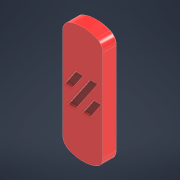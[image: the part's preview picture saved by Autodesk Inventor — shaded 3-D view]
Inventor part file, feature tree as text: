
AUTODESK INVENTOR PART (.ipt)
format: ipt  version: 2022.1 (Build 261234000, 234)  size: 317,440 bytes
history: native  units: mm
features: sketch x8, extrude x7, projected_geometry x6, direct_edit x5, move_body x5, reference x4, other x3, hole x2, chamfer x2, fillet x1, plane x1, delete_face x1
ambient origin geometry x8: Origin, YZ Plane, XZ Plane, XY Plane, X Axis, Y Axis, Z Axis, Center Point
bodies: Volumenkörper1 (feature_tree)
feature tree (45):
  extrude  "Extrusion1"  Depth=4.0mm TaperAngle=0.0deg
  extrude  "Extrusion2"  Depth=3.2mm
  hole  "Bohrung1"  [1 undecoded]
  sketch  "Skizze4"  dims[d109=2.156321mm d110=2.156321mm]
  direct_edit  "Direktbearbeitung1"
  fillet  "Rundung2"  Radius=12.398846mm
  extrude  "Extrusion4"  Depth=2.156321mm
  extrude  "Extrusion5"  Depth=2.479769mm
  extrude  "Extrusion6"  Depth=6.199423mm
  direct_edit  "Direktbearbeitung2"
  direct_edit  "Direktbearbeitung4"
  direct_edit  "Direktbearbeitung5"
  chamfer  "Fase11"  Distance=15.5mm
  plane  "Arbeitsebene1"
  extrude  "Extrusion7"  Depth=0.2mm
  direct_edit  "Direktbearbeitung6"
  hole  "Bohrung2"  [1 undecoded]
  chamfer  "Fase12"  Distance=3.5mm
  extrude  "Extrusion8"  Depth=0.8mm TaperAngle=0.0deg
  delete_face  "Fläche löschen3"
  sketch  "Skizze1"  dims[d0=4.0mm d1=0.0mm d3=3.1mm d4=0.0mm]
  reference  "Referenz1"
  sketch  "Skizze2"  dims[d5=5.6mm d6=6.0mm d7=7.1mm d8=1.2mm d9=90.0deg d10=3.2mm d11=0.0mm d89=5.6mm]
  reference  "Referenz2"
  sketch  "Skizze3"  dims[d104=5.6mm d107=14.217391mm d108=12.398846mm]
  reference  "Referenz3"
  projected_geometry  "Projizierte Kontur1"
  sketch  "Skizze5"  dims[d111=2.479769mm d112=2.479769mm]
  reference  "Referenz4"
  sketch  "Skizze6"  dims[d113=2.479769mm d114=6.199423mm]
  projected_geometry  "Projizierte Kontur2"
  projected_geometry  "Projizierte Kontur3"
  sketch  "Skizze7"  dims[d115=6.199423mm]
  projected_geometry  "Projizierte Kontur4"
  sketch  "Skizze8"  dims[d116=6.199423mm d117=15.5mm d118=0.641304mm d121=0.0mm d122=0.0mm d123=0.5mm d124=3.5mm d125=0.8mm d126=0.0mm d127=0.0mm d128=0.0mm d129=1.4mm d130=0.0mm d149=0.0mm d150=0.0mm d151=1.0mm d155=0.0mm d156=0.0mm d157=1.5mm d170=0.0mm d171=0.0mm d172=1.0mm d173=0.4mm d174=2.0mm d175=45.0deg d176=4.8mm d177=4.8mm d178=0.0mm d179=0.0mm d180=0.0mm d181=0.0mm d182=0.75mm d183=6.5mm d184=6.0mm d185=7.5mm d186=1.4mm d187=90.0deg d188=4.0mm d189=0.0mm d190=0.5mm d191=2.0mm d192=45.0deg d193=0.2mm d194=0.0mm]
  projected_geometry  "Projizierte Kontur5"
  projected_geometry  "Projizierte Kontur6"
  other  "<userpath>\Desktop\Voron-2-2.4r1\Custom\Front_Idlers\Baugruppe1.iam"
  other  "Baugruppe1.iam"
  other  "Cover1:1"
  move_body  "Verschieben1"
  move_body  "Verschieben2"
  move_body  "Verschieben4"
  move_body  "Verschieben5"
  move_body  "Verschieben6"
note: 2 required parameter values undecoded (feature->parameter linkage not recoverable at this tier; creation-order binding heuristic only, values carry confidence <= 0.55)
